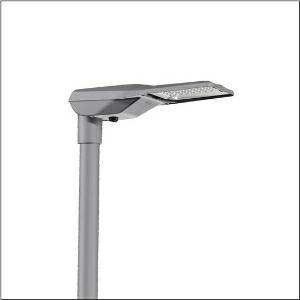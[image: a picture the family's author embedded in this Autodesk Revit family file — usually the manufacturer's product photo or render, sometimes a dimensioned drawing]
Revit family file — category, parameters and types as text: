
# Revit family: streetlight_sl_21_mini___p0_8a_5xe2u33r08jb_f297
name_source: partatom
category: Lighting Fixtures
units: mm (PartAtom-declared; Revit-internal decimal feet)

## family parameters
Cut with Voids When Loaded = No
Host = Face
Light Source = No
Part Type = Normal
Room Calculation Point = No
Round Connector Dimension = Use Diameter
Shared = No

## types (1)
- --- (1 x LED, 13050 lm, 88.6 W, 3000K)
    Apparent Load = 89 VA
    CIE Flux Codes = 36 69 97 100 100
    Color Rendering = 70
    Color Temperature = 3000K
    Default Elevation = 1800 mm
    Description = Streetlight SL 21 mini, mast luminaire, primary light control with lens, of PMMA, primary optical cover: cover, of toughened safety glass, transparent, light distribution: P0.8a, light emission: direct distribution, primary light characteristic: asymmetric, installation type: post-top, side-entry, LED, High Power LED, rated luminous flux: 13.050lm, luminous efficacy: 147lm/W, light colour: 730, colour temperature: 3000K, control gear: D4i, control: pre-setting: logarithmic dimming characteristic, flexible luminous flux parameterisation, time-dependent luminous flux control, constant luminous flux control, overheat protection, mains connection: 220..240V, AC, 50/60Hz, start of lifetime: 89W, end of service life: 92W, reduction: 41W, luminaire housing, of diecast aluminium, powder-coated, SITECO metallic grey (DB 702S), corrosivity category C5 high according to DIN EN ISO 12944, multi-level sealing system, sealing non-destructively replaceable, inclination adjustable: 0°, 5°, 10°, 15°, please order mast flange separately, length: 628mm, width: 235mm, height: 110mm, mast flange for spigot size: 42mm (side-entry): 5XC10008XM4, 60/48mm (side-entry/post-top): 5XC10108XM2, 76/60mm (side-entry/post-top): 5XC10108XM1, mounting height: 4..8m, Smart Interface below, protection rating (complete): IP66, insulation class (complete): insulation class II (safety insulation), certification: CE, ENEC, ENEC+, VDE, impact resistance: IK10, permissible operating ambient temperature for outdoor applications: -40..+50°C, standard-compliant lighting for roads and squares, packaging unit: 1 piece

Light Distribution: P0.8a
    Height = 110 mm
    Lamp = 1 x LED
    Lamp Light Flux = 13050 lm
    Lamp Power = 88.6 W
    Lamp count = 1
    Length = 625 mm
    Luminous efficacy = 147 lm/W
    Manufacturer = Siteco
    ModVariant = No
    Model = 5XE2U33R08JB
    Number of Poles = 1
    OnlyDefault = Yes
    Power Factor = 1
    Product Name = Streetlight SL 21 mini | P0.8a
    Product group = mast luminaire | pylon top
    ProductGroupID = 6100
    Protection Class = Protection class II
    Protection Degree = IP 66
    RLX_Detail_Level = 1
    RLX_Emergency_Light_Flux = 0 lm
    RLX_Emergency_Type = 0
    RLX_Emergency_Type_DB = No
    RlxData = <blob elided: 26169 chars, md5=1ae9c0e9>
    Socket = socket
    Standby Power = 0 W
    System Light Flux = 13050 lm
    System Power = 89 W
    Type Comments = factory setting: luminous flux: 100 % | dim-lin: 254 | 915 mA
    Type Image = l_1003516.jpg
    URL = http://relux.com
    VarID = @adj_033115
    Voltage = 0 V
    Weight = 0.00 kg
    Width = 234 mm

## geometry (parser evidence)
native form markers: Blend x4, Sweep x12
no freeform markers — native parametric forms only
